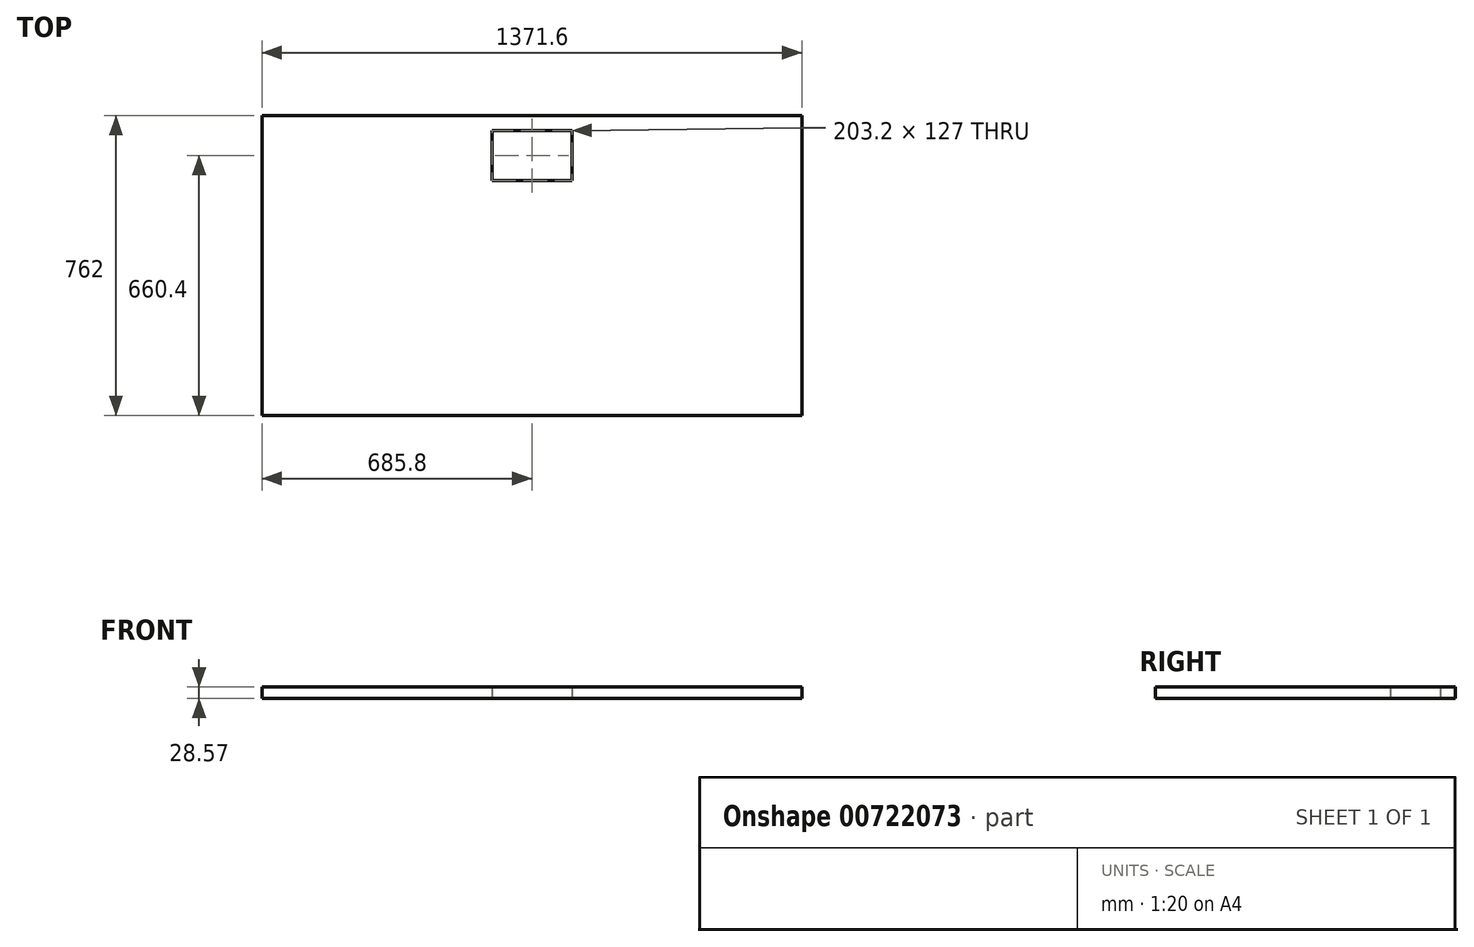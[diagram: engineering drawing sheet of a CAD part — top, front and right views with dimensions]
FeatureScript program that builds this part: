
annotation { "Feature Type Name" : "Feature", "Feature Type Description" : "" }
export const myFeature = defineFeature(function(context is Context, id is Id, definition is map)
    precondition{}
    {
        {
            var Q0;
            Q0=qCreatedBy(makeId("Top.planeOp"),FACE);
            var sketch = newSketch(context, id + "F0", { "sketchPlane" : qUnion([Q0])});
            skLineSegment(sketch, "E0.bottom", {"start": v(685.8, 381) * mm, "end": v(-685.8, 381) * mm});
            skLineSegment(sketch, "E0.top", {"start": v(685.8, -381) * mm, "end": v(-685.8, -381) * mm});
            skLineSegment(sketch, "E0.left", {"start": v(685.8, 381) * mm, "end": v(685.8, -381) * mm});
            skLineSegment(sketch, "E0.right", {"start": v(-685.8, 381) * mm, "end": v(-685.8, -381) * mm});
            skPoint(sketch, "E0.middle", {"position": v(0, 0) * mm});
            skLineSegment(sketch, "E1", {"start": v(0, 381) * mm, "end": v(0, 279.4) * mm});
            skLineSegment(sketch, "E2.bottom", {"start": v(101.6, 215.9) * mm, "end": v(-101.6, 215.9) * mm});
            skLineSegment(sketch, "E2.top", {"start": v(101.6, 342.9) * mm, "end": v(-101.6, 342.9) * mm});
            skLineSegment(sketch, "E2.left", {"start": v(101.6, 215.9) * mm, "end": v(101.6, 342.9) * mm});
            skLineSegment(sketch, "E2.right", {"start": v(-101.6, 215.9) * mm, "end": v(-101.6, 342.9) * mm});
            skPoint(sketch, "E2.middle", {"position": v(0, 279.4) * mm});
            skSolve(sketch);
        }
        {
            var Q0;
            Q0=makeQuery(id+"F0.imprint","IMPRINT",FACE,{"disambiguationData":[TD([[makeQuery(id+"F0.imprint","IMPRINT",EDGE,{"derivedFrom":sQuery(id+"F0.wireOp",EDGE,"E0.bottom")}),1.0]])]});
            extrude(context, id + "F1", {"entities" : qUnion([Q0]), "depth" : 28.57 * mm, "offsetDistance" : 25.4 * mm});
        }
    });
